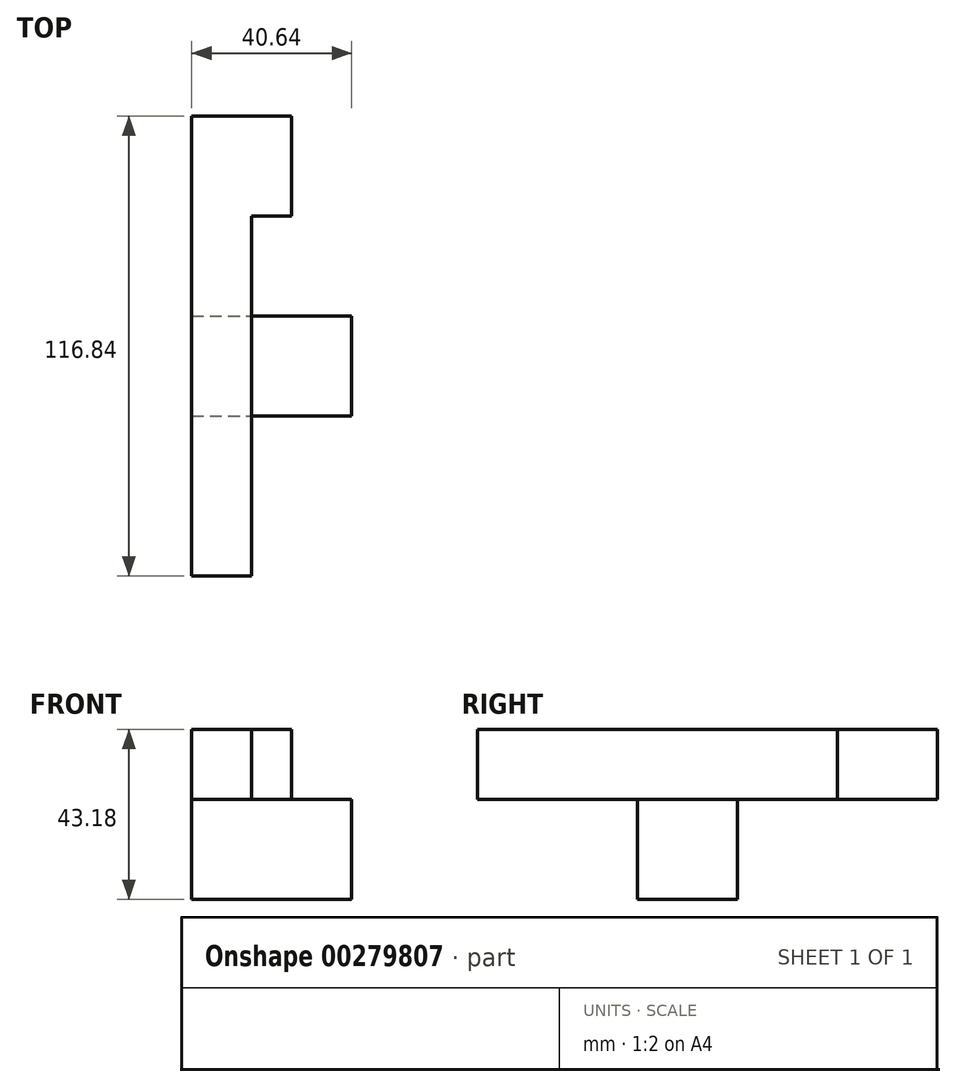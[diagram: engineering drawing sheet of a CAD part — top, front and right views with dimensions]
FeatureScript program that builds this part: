
annotation { "Feature Type Name" : "Feature", "Feature Type Description" : "" }
export const myFeature = defineFeature(function(context is Context, id is Id, definition is map)
    precondition{}
    {
        {
            var Q0;
            Q0=qCreatedBy(makeId("Right.planeOp"),FACE);
            var sketch = newSketch(context, id + "F0", { "sketchPlane" : qUnion([Q0])});
            skLineSegment(sketch, "E0.bottom", {"start": v(57.9, 53.62) * mm, "end": v(-58.95, 53.62) * mm});
            skLineSegment(sketch, "E0.top", {"start": v(57.9, 35.84) * mm, "end": v(-58.95, 35.84) * mm});
            skLineSegment(sketch, "E0.left", {"start": v(57.9, 53.62) * mm, "end": v(57.9, 35.84) * mm});
            skLineSegment(sketch, "E0.right", {"start": v(-58.95, 53.62) * mm, "end": v(-58.95, 35.84) * mm});
            skSolve(sketch);
        }
        {
            var Q0;
            Q0=makeQuery(id+"F0.imprint","IMPRINT",FACE,{"disambiguationData":[TD([[makeQuery(id+"F0.imprint","IMPRINT",EDGE,{"derivedFrom":sQuery(id+"F0.wireOp",EDGE,"E0.bottom")}),1.0]])]});
            extrude(context, id + "F1", {"entities" : qUnion([Q0]), "oppositeDirection" : true, "depth" : 15.24 * mm});
        }
        {
            var Q0;
            Q0=makeQuery(id+"F1.opExtrude","CAP_FACE",FACE,{"disambiguationData":[OSD([sQuery(id+"F0.wireOp",EDGE,"E0.bottom"),sQuery(id+"F0.wireOp",EDGE,"E0.top"),sQuery(id+"F0.wireOp",EDGE,"E0.left"),sQuery(id+"F0.wireOp",EDGE,"E0.right")])],"isStart":true});
            var sketch = newSketch(context, id + "F2", { "sketchPlane" : qUnion([Q0])});
            skLineSegment(sketch, "E1", {"start": v(32.5, 53.62) * mm, "end": v(32.5, 35.84) * mm});
            skSolve(sketch);
        }
        {
            var Q0;
            {var subQ0=sQuery(id+"F2.wireOp",EDGE,"E1");Q0=makeQuery(id+"F2.imprint","IMPRINT",FACE,{"disambiguationData":[TD([[makeQuery(id+"F2.imprint","IMPRINT",EDGE,{"derivedFrom":subQ0}),1.0]])]});}
            extrude(context, id + "F3", {"entities" : qUnion([Q0]), "operationType" : NewBodyOperationType.ADD, "depth" : 10.16 * mm});
        }
        {
            var Q0;
            {var subQ0=sQuery(id+"F0.wireOp",EDGE,"E0.top");Q0=makeQuery(id+"F3.boolean.opBoolean","MERGE",FACE,{"derivedFrom":[makeQuery(id+"F1.opExtrude","SWEPT_FACE",FACE,{"disambiguationData":[OSD([subQ0])]}),makeQuery(id+"F3.opExtrude","SWEPT_FACE",FACE,{"disambiguationData":[OSD([subQ0])]})]});}
            var sketch = newSketch(context, id + "F4", { "sketchPlane" : qUnion([Q0])});
            skLineSegment(sketch, "E2", {"start": v(-15.24, 18.3) * mm, "end": v(0, 18.3) * mm});
            skLineSegment(sketch, "E3", {"start": v(-15.24, -7.1) * mm, "end": v(0, -7.1) * mm});
            skSolve(sketch);
        }
        {
            var Q0;
            {var subQ0=sQuery(id+"F4.wireOp",EDGE,"E2");Q0=makeQuery(id+"F4.imprint","IMPRINT",FACE,{"disambiguationData":[TD([[makeQuery(id+"F4.imprint","IMPRINT",EDGE,{"derivedFrom":subQ0}),-1.0]])]});}
            extrude(context, id + "F5", {"entities" : qUnion([Q0]), "operationType" : NewBodyOperationType.ADD, "depth" : 25.4 * mm});
        }
        {
            var Q0;
            {var subQ0=sQuery(id+"F0.wireOp",EDGE,"E0.top");var subQ1=makeQuery(id+"F1.opExtrude","CAP_EDGE",EDGE,{"disambiguationData":[OSD([subQ0])],"isStart":true});Q0=makeQuery(id+"F5.boolean.opBoolean","MERGE",FACE,{"derivedFrom":[makeQuery(id+"F1.opExtrude","CAP_FACE",FACE,{"disambiguationData":[OSD([sQuery(id+"F0.wireOp",EDGE,"E0.bottom"),subQ0,sQuery(id+"F0.wireOp",EDGE,"E0.left"),sQuery(id+"F0.wireOp",EDGE,"E0.right")])],"isStart":true}),makeQuery(id+"F5.opExtrude","SWEPT_FACE",FACE,{"disambiguationData":[OSD([subQ0]),TDD([makeQuery(id+"F4.imprint","IMPRINT",EDGE,{"disambiguationData":[TD([[makeQuery(id+"F4.imprint","INTERSECT",VERTEX,{"derivedFrom":[subQ1,sQuery(id+"F4.wireOp",EDGE,"E2")]}),1.0]])],"derivedFrom":subQ1})])]})]});}
            var sketch = newSketch(context, id + "F6", { "sketchPlane" : qUnion([Q0])});
            skLineSegment(sketch, "E4", {"start": v(-18.3, 35.84) * mm, "end": v(7.1, 35.84) * mm});
            skSolve(sketch);
        }
        {
            var Q0;
            Q0=makeQuery(id+"F6.imprint","IMPRINT",FACE,{"disambiguationData":[TD([[makeQuery(id+"F6.imprint","IMPRINT",EDGE,{"derivedFrom":sQuery(id+"F6.wireOp",EDGE,"E4")}),-1.0]])]});
            extrude(context, id + "F7", {"entities" : qUnion([Q0]), "operationType" : NewBodyOperationType.ADD, "depth" : 25.4 * mm});
        }
    });
